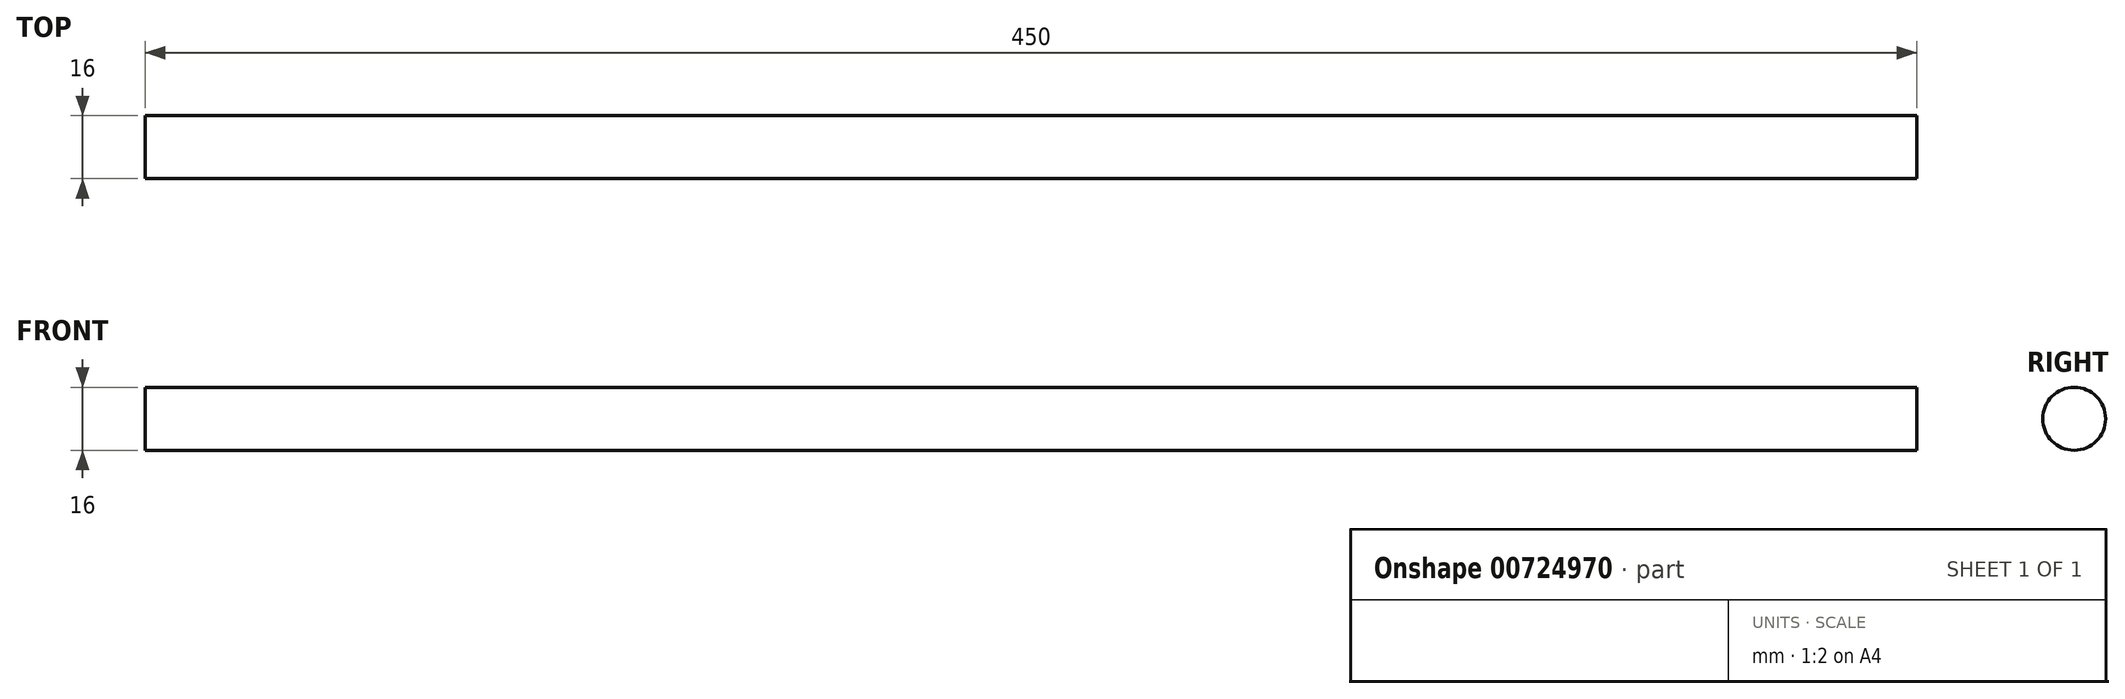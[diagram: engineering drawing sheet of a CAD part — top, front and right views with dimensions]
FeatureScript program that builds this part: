
annotation { "Feature Type Name" : "Feature", "Feature Type Description" : "" }
export const myFeature = defineFeature(function(context is Context, id is Id, definition is map)
    precondition{}
    {
        {
            var Q0;
            Q0=qCreatedBy(makeId("Right.planeOp"),FACE);
            var sketch = newSketch(context, id + "F0", { "sketchPlane" : qUnion([Q0])});
            skCircle(sketch, "E0", {"center": v(0, 0) * mm, "radius": 8 * mm});
            skCircle(sketch, "E1.0", {"center": v(0, 0) * mm, "radius": 7.7 * mm, "construction": true});
            skSolve(sketch);
        }
        {
            var Q0;
            Q0=qSketchRegion(id+"F0",true);
            var Q1;
            Q1=sQuery(id+"F0.wireOp",EDGE,"E0");
            extrude(context, id + "F1", {"entities" : qUnion([Q0]), "bodyType" : ToolBodyType.SURFACE, "surfaceEntities" : qUnion([Q1]), "depth" : 450 * mm, "offsetDistance" : 25 * mm, "symmetric" : true});
        }
    });
